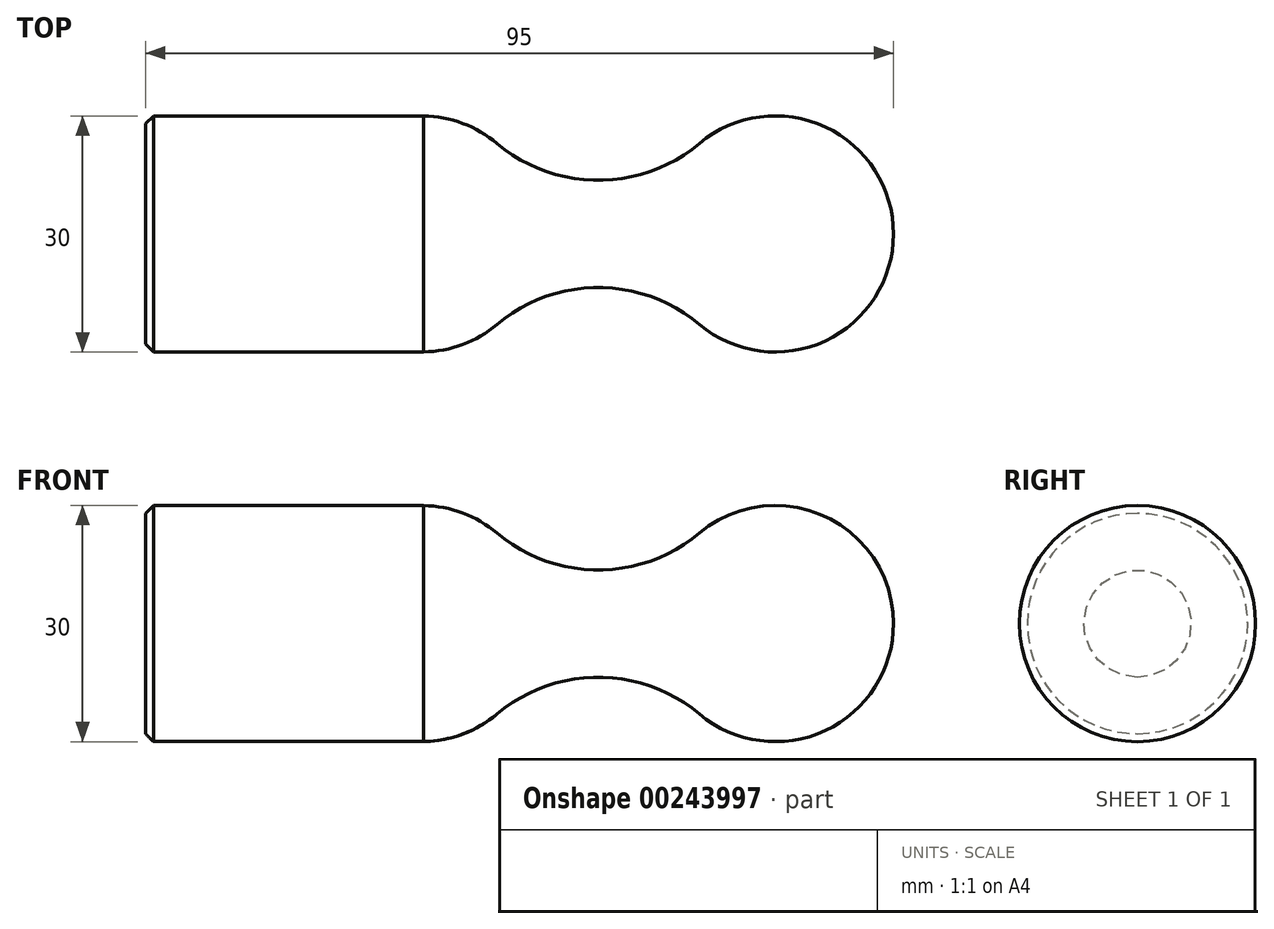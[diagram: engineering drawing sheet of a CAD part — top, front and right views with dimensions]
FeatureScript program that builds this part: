
annotation { "Feature Type Name" : "Feature", "Feature Type Description" : "" }
export const myFeature = defineFeature(function(context is Context, id is Id, definition is map)
    precondition{}
    {
        {
            var Q0;
            Q0=qCreatedBy(makeId("Front.planeOp"),FACE);
            var sketch = newSketch(context, id + "F0", { "sketchPlane" : qUnion([Q0])});
            skArc(sketch, "E0", {"start": v(0, 0) * mm, "mid": v(-8.66, 13.6) * mm, "end": v(-24.64, 11.49) * mm});
            skArc(sketch, "E1", {"start": v(-50.36, 11.49) * mm, "mid": v(-55.02, 14.15) * mm, "end": v(-60.33, 15) * mm});
            skArc(sketch, "E2", {"start": v(-50.36, 11.49) * mm, "mid": v(-37.5, 6.8) * mm, "end": v(-24.64, 11.49) * mm});
            skLineSegment(sketch, "E3", {"start": v(-59.67, 15) * mm, "end": v(-95, 15) * mm});
            skLineSegment(sketch, "E4", {"start": v(0, 0) * mm, "end": v(-94.95, 0) * mm});
            skLineSegment(sketch, "E5", {"start": v(-95, 15) * mm, "end": v(-94.95, 0) * mm});
            skSolve(sketch);
        }
        {
            var Q0;
            Q0=makeQuery(id+"F0.imprint","IMPRINT",FACE,{"disambiguationData":[TD([[makeQuery(id+"F0.imprint","IMPRINT",EDGE,{"derivedFrom":sQuery(id+"F0.wireOp",EDGE,"E0")}),1.0]])]});
            var Q1;
            Q1=sQuery(id+"F0.wireOp",EDGE,"E4");
            revolve(context, id + "F1", {"entities" : qUnion([Q0]), "axis" : qUnion([Q1]), "revolveType" : RevolveType.FULL});
        }
        {
            var Q0;
            Q0=makeQuery(id+"F1.opRevolve","SWEPT_EDGE",EDGE,{"disambiguationData":[OSD([sQuery(id+"F0.wireOp",EDGE,"E3"),sQuery(id+"F0.wireOp",EDGE,"E5")])]});
            chamfer(context, id + "F2", {"entities" : qUnion([Q0]), "width" : 1 * mm, "tangentPropagation" : true});
        }
    });
